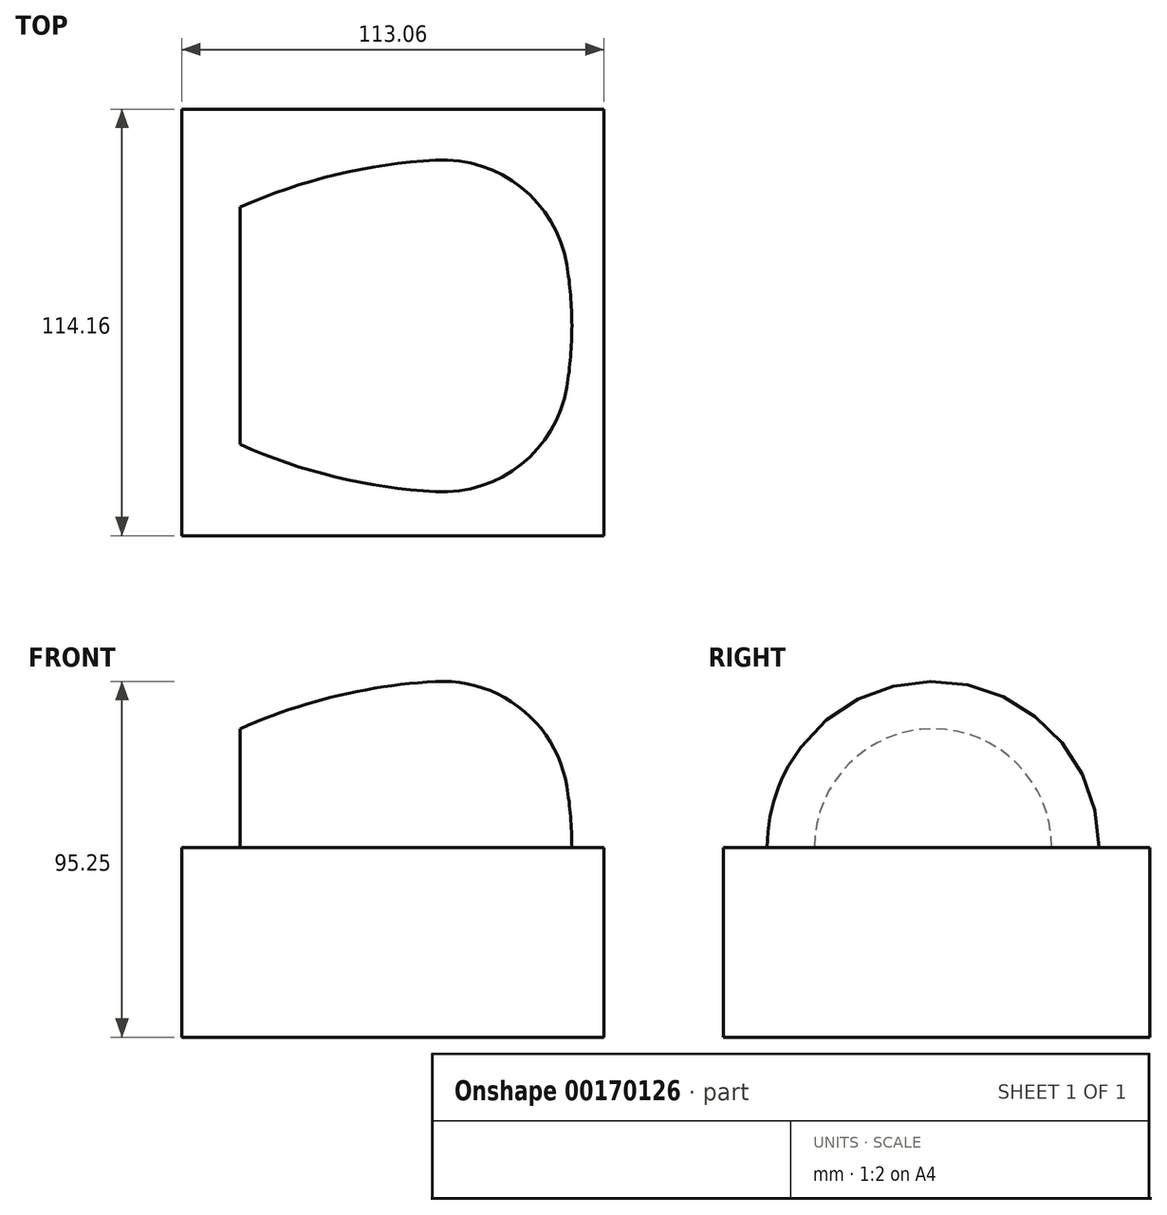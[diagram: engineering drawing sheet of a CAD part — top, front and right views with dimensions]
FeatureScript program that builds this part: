
annotation { "Feature Type Name" : "Feature", "Feature Type Description" : "" }
export const myFeature = defineFeature(function(context is Context, id is Id, definition is map)
    precondition{}
    {
        {
            var Q0;
            Q0=qCreatedBy(makeId("Top.planeOp"),FACE);
            var sketch = newSketch(context, id + "F0", { "sketchPlane" : qUnion([Q0])});
            skLineSegment(sketch, "E0", {"start": v(0, 0) * mm, "end": v(88.9, 0) * mm, "construction": true});
            skLineSegment(sketch, "E1", {"start": v(0, 0) * mm, "end": v(0, -31.75) * mm, "construction": true});
            skLineSegment(sketch, "E2", {"start": v(0, -31.75) * mm, "end": v(88.9, -31.75) * mm, "construction": true});
            skLineSegment(sketch, "E3", {"start": v(0, 0) * mm, "end": v(0, 12.7) * mm, "construction": true});
            skLineSegment(sketch, "E4", {"start": v(0, 12.7) * mm, "end": v(88.9, 12.7) * mm, "construction": true});
            skLineSegment(sketch, "E5", {"start": v(88.9, -31.75) * mm, "end": v(88.9, 12.7) * mm, "construction": true});
            skArc(sketch, "E6", {"start": v(88.9, -31.75) * mm, "mid": v(88.56, -23.58) * mm, "end": v(87.55, -15.46) * mm});
            skLineSegment(sketch, "E7", {"start": v(0, 0) * mm, "end": v(0, -31.75) * mm});
            skLineSegment(sketch, "E8", {"start": v(88.9, -31.75) * mm, "end": v(0, -31.75) * mm});
            skArc(sketch, "E9", {"start": v(87.55, -15.46) * mm, "mid": v(75.37, 5.3) * mm, "end": v(52.43, 12.65) * mm});
            skArc(sketch, "E10", {"start": v(52.43, 12.65) * mm, "mid": v(25.64, 8.7) * mm, "end": v(0, 0) * mm});
            skSolve(sketch);
        }
        {
            var Q0;
            Q0=makeQuery(id+"F0.imprint","IMPRINT",FACE,{"disambiguationData":[TD([[makeQuery(id+"F0.imprint","IMPRINT",EDGE,{"derivedFrom":sQuery(id+"F0.wireOp",EDGE,"E6")}),1.0]])]});
            var Q1;
            Q1=sQuery(id+"F0.wireOp",EDGE,"E8");
            revolve(context, id + "F1", {"entities" : qUnion([Q0]), "axis" : qUnion([Q1]), "revolveType" : RevolveType.FULL});
        }
        {
            var Q0;
            Q0=qCreatedBy(makeId("Top.planeOp"),FACE);
            var sketch = newSketch(context, id + "F2", { "sketchPlane" : qUnion([Q0])});
            skLineSegment(sketch, "E11.bottom", {"start": v(-15.57, 26.27) * mm, "end": v(97.5, 26.27) * mm});
            skLineSegment(sketch, "E11.top", {"start": v(-15.57, -87.9) * mm, "end": v(97.5, -87.9) * mm});
            skLineSegment(sketch, "E11.left", {"start": v(-15.57, 26.27) * mm, "end": v(-15.57, -87.9) * mm});
            skLineSegment(sketch, "E11.right", {"start": v(97.5, 26.27) * mm, "end": v(97.5, -87.9) * mm});
            skSolve(sketch);
        }
        {
            var Q0;
            Q0=qSketchRegion(id+"F2",true);
            extrude(context, id + "F3", {"entities" : qUnion([Q0]), "operationType" : NewBodyOperationType.ADD, "oppositeDirection" : true, "depth" : 50.8 * mm});
        }
    });
